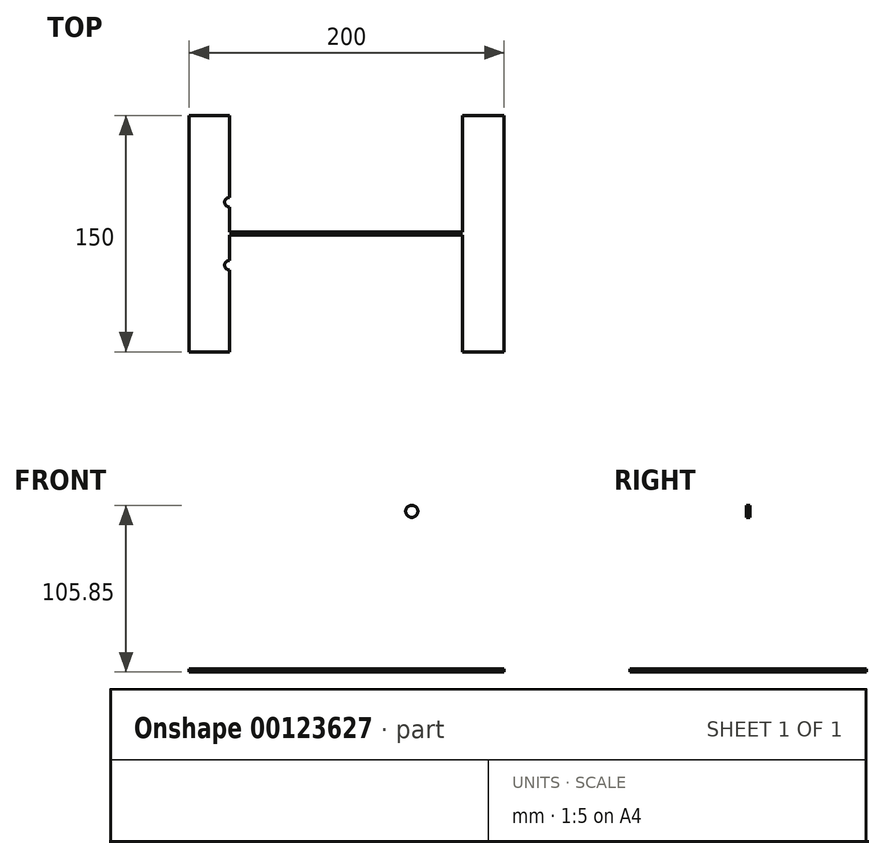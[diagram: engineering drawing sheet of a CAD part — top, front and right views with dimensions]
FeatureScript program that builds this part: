
annotation { "Feature Type Name" : "Feature", "Feature Type Description" : "" }
export const myFeature = defineFeature(function(context is Context, id is Id, definition is map)
    precondition{}
    {
        {
            var Q0;
            Q0=qCreatedBy(makeId("Top.planeOp"),FACE);
            var sketch = newSketch(context, id + "F0", { "sketchPlane" : qUnion([Q0])});
            skLineSegment(sketch, "E0.bottom", {"start": v(-99.5, 63.3) * mm, "end": v(100.5, 63.3) * mm});
            skLineSegment(sketch, "E0.top", {"start": v(-99.5, -86.7) * mm, "end": v(100.5, -86.7) * mm});
            skLineSegment(sketch, "E0.left", {"start": v(-99.5, 63.3) * mm, "end": v(-99.5, -86.7) * mm});
            skLineSegment(sketch, "E0.right", {"start": v(100.5, 63.3) * mm, "end": v(100.5, -86.7) * mm});
            skSolve(sketch);
        }
        {
            var Q0;
            Q0=makeQuery(id+"F0.imprint","IMPRINT",FACE,{"disambiguationData":[TD([[makeQuery(id+"F0.imprint","IMPRINT",EDGE,{"derivedFrom":sQuery(id+"F0.wireOp",EDGE,"E0.bottom")}),-1.0]])]});
            extrude(context, id + "F1", {"entities" : qUnion([Q0]), "depth" : 2 * mm});
        }
        {
            var Q0;
            Q0=makeQuery(id+"F1.opExtrude","CAP_FACE",FACE,{"disambiguationData":[OSD([sQuery(id+"F0.wireOp",EDGE,"E0.bottom"),sQuery(id+"F0.wireOp",EDGE,"E0.top"),sQuery(id+"F0.wireOp",EDGE,"E0.left"),sQuery(id+"F0.wireOp",EDGE,"E0.right")])],"isStart":false});
            var sketch = newSketch(context, id + "F2", { "sketchPlane" : qUnion([Q0])});
            skLineSegment(sketch, "E1.bottom", {"start": v(-99.5, 63.3) * mm, "end": v(-99.5, 63.3) * mm});
            skLineSegment(sketch, "E1.top", {"start": v(-99.5, -86.7) * mm, "end": v(-99.5, -86.7) * mm});
            skLineSegment(sketch, "E1.left", {"start": v(-99.5, 63.3) * mm, "end": v(-99.5, -86.7) * mm});
            skLineSegment(sketch, "E1.right", {"start": v(-99.5, 63.3) * mm, "end": v(-99.5, -86.7) * mm});
            skLineSegment(sketch, "E2.bottom", {"start": v(100.5, -86.7) * mm, "end": v(-99.5, -86.7) * mm});
            skLineSegment(sketch, "E2.top", {"start": v(100.5, 63.3) * mm, "end": v(-99.5, 63.3) * mm});
            skLineSegment(sketch, "E2.left", {"start": v(100.5, -86.7) * mm, "end": v(100.5, 63.3) * mm});
            skLineSegment(sketch, "E2.right", {"start": v(-99.5, -86.7) * mm, "end": v(-99.5, 63.3) * mm});
            skLineSegment(sketch, "E3", {"start": v(100.5, -11.7) * mm, "end": v(100.5, 8.3) * mm});
            skLineSegment(sketch, "E4", {"start": v(100.5, 8.3) * mm, "end": v(-99.5, 8.3) * mm});
            skLineSegment(sketch, "E5.MirrorCS", {"start": v(100.5, -31.7) * mm, "end": v(-99.5, -31.7) * mm});
            skLineSegment(sketch, "E6", {"start": v(74, 63.3) * mm, "end": v(74, -86.7) * mm});
            skLineSegment(sketch, "E7.MirrorCS", {"start": v(-74, 63.3) * mm, "end": v(-74, -86.7) * mm});
            skCircle(sketch, "E8", {"center": v(74, 8.3) * mm, "radius": 3 * mm});
            skCircle(sketch, "E9", {"center": v(74, -31.7) * mm, "radius": 3 * mm});
            skCircle(sketch, "E10.MirrorC", {"center": v(-74, -31.7) * mm, "radius": 3 * mm});
            skCircle(sketch, "E11.MirrorC", {"center": v(-74, 8.3) * mm, "radius": 3 * mm});
            skLineSegment(sketch, "E12.bottom", {"start": v(-99.5, -10.7) * mm, "end": v(100.5, -10.7) * mm});
            skLineSegment(sketch, "E12.top", {"start": v(-99.5, -12.7) * mm, "end": v(100.5, -12.7) * mm});
            skLineSegment(sketch, "E12.left", {"start": v(-99.5, -10.7) * mm, "end": v(-99.5, -12.7) * mm});
            skLineSegment(sketch, "E12.right", {"start": v(100.5, -10.7) * mm, "end": v(100.5, -12.7) * mm});
            skSolve(sketch);
        }
        {
            var Q0;
            {var subQ0=sQuery(id+"F2.wireOp",EDGE,"E12.bottom");var subQ1=sQuery(id+"F2.wireOp",EDGE,"E7.MirrorCS");var subQ2=makeQuery(id+"F2.imprint","INTERSECT",VERTEX,{"derivedFrom":[subQ1,subQ0]});Q0=makeQuery(id+"F2.imprint","IMPRINT",FACE,{"disambiguationData":[TD([[makeQuery(id+"F2.imprint","IMPRINT",EDGE,{"disambiguationData":[TD([[subQ2,-1.0]])],"derivedFrom":subQ1}),1.0]])]});}
            var Q1;
            {var subQ0=sQuery(id+"F2.wireOp",EDGE,"E12.bottom");var subQ1=sQuery(id+"F2.wireOp",EDGE,"E6");var subQ2=makeQuery(id+"F2.imprint","INTERSECT",VERTEX,{"derivedFrom":[subQ1,subQ0]});Q1=makeQuery(id+"F2.imprint","IMPRINT",FACE,{"disambiguationData":[TD([[makeQuery(id+"F2.imprint","IMPRINT",EDGE,{"disambiguationData":[TD([[subQ2,-1.0]])],"derivedFrom":subQ1}),1.0]])]});}
            var Q2;
            {var subQ5=sQuery(id+"F2.wireOp",EDGE,"E12.left");Q2=makeQuery(id+"F2.imprint","IMPRINT",FACE,{"disambiguationData":[TD([[makeQuery(id+"F2.imprint","IMPRINT",EDGE,{"derivedFrom":subQ5}),1.0]])]});}
            extrude(context, id + "F3", {"entities" : qUnion([Q0, Q1, Q2]), "operationType" : NewBodyOperationType.ADD, "depth" : 300 * mm});
        }
        {
            var Q0;
            Q0=makeQuery(id+"F3.opExtrude","SWEPT_FACE",FACE,{"disambiguationData":[OSD([sQuery(id+"F2.wireOp",EDGE,"E12.top")])]});
            var sketch = newSketch(context, id + "F4", { "sketchPlane" : qUnion([Q0])});
            skSolve(sketch);
        }
        {
            var Q0;
            {var subQ0=sQuery(id+"F2.wireOp",EDGE,"E10.MirrorC");var subQ1=sQuery(id+"F2.wireOp",EDGE,"E5.MirrorCS");var subQ2=makeQuery(id+"F2.imprint","INTERSECT",VERTEX,{"disambiguationData":[OD(0.0)],"derivedFrom":[subQ1,subQ0]});Q0=makeQuery(id+"F2.imprint","IMPRINT",FACE,{"disambiguationData":[TD([[makeQuery(id+"F2.imprint","IMPRINT",EDGE,{"disambiguationData":[TD([[subQ2,-1.0]])],"derivedFrom":subQ1}),1.0]])]});}
            var Q1;
            {var subQ0=sQuery(id+"F2.wireOp",EDGE,"E10.MirrorC");var subQ1=sQuery(id+"F2.wireOp",EDGE,"E5.MirrorCS");var subQ2=makeQuery(id+"F2.imprint","INTERSECT",VERTEX,{"disambiguationData":[OD(0.0)],"derivedFrom":[subQ1,subQ0]});Q1=makeQuery(id+"F2.imprint","IMPRINT",FACE,{"disambiguationData":[TD([[makeQuery(id+"F2.imprint","IMPRINT",EDGE,{"disambiguationData":[TD([[subQ2,-1.0]])],"derivedFrom":subQ1}),-1.0]])]});}
            var Q2;
            {var subQ0=sQuery(id+"F2.wireOp",EDGE,"E7.MirrorCS");var subQ1=sQuery(id+"F2.wireOp",EDGE,"E5.MirrorCS");var subQ2=makeQuery(id+"F2.imprint","INTERSECT",VERTEX,{"derivedFrom":[subQ1,subQ0]});Q2=makeQuery(id+"F2.imprint","IMPRINT",FACE,{"disambiguationData":[TD([[makeQuery(id+"F2.imprint","IMPRINT",EDGE,{"disambiguationData":[TD([[subQ2,-1.0]])],"derivedFrom":subQ1}),-1.0]])]});}
            var Q3;
            {var subQ0=sQuery(id+"F2.wireOp",EDGE,"E7.MirrorCS");var subQ1=sQuery(id+"F2.wireOp",EDGE,"E5.MirrorCS");var subQ2=makeQuery(id+"F2.imprint","INTERSECT",VERTEX,{"derivedFrom":[subQ1,subQ0]});Q3=makeQuery(id+"F2.imprint","IMPRINT",FACE,{"disambiguationData":[TD([[makeQuery(id+"F2.imprint","IMPRINT",EDGE,{"disambiguationData":[TD([[subQ2,-1.0]])],"derivedFrom":subQ1}),1.0]])]});}
            var Q4;
            {var subQ0=sQuery(id+"F2.wireOp",EDGE,"E6");var subQ1=sQuery(id+"F2.wireOp",EDGE,"E5.MirrorCS");var subQ2=makeQuery(id+"F2.imprint","INTERSECT",VERTEX,{"derivedFrom":[subQ1,subQ0]});Q4=makeQuery(id+"F2.imprint","IMPRINT",FACE,{"disambiguationData":[TD([[makeQuery(id+"F2.imprint","IMPRINT",EDGE,{"disambiguationData":[TD([[subQ2,-1.0]])],"derivedFrom":subQ1}),-1.0]])]});}
            var Q5;
            {var subQ0=sQuery(id+"F2.wireOp",EDGE,"E6");var subQ1=sQuery(id+"F2.wireOp",EDGE,"E5.MirrorCS");var subQ2=makeQuery(id+"F2.imprint","INTERSECT",VERTEX,{"derivedFrom":[subQ1,subQ0]});Q5=makeQuery(id+"F2.imprint","IMPRINT",FACE,{"disambiguationData":[TD([[makeQuery(id+"F2.imprint","IMPRINT",EDGE,{"disambiguationData":[TD([[subQ2,-1.0]])],"derivedFrom":subQ1}),1.0]])]});}
            var Q6;
            {var subQ0=sQuery(id+"F2.wireOp",EDGE,"E9");var subQ1=sQuery(id+"F2.wireOp",EDGE,"E5.MirrorCS");var subQ2=makeQuery(id+"F2.imprint","INTERSECT",VERTEX,{"disambiguationData":[OD(0.0)],"derivedFrom":[subQ1,subQ0]});Q6=makeQuery(id+"F2.imprint","IMPRINT",FACE,{"disambiguationData":[TD([[makeQuery(id+"F2.imprint","IMPRINT",EDGE,{"disambiguationData":[TD([[subQ2,-1.0]])],"derivedFrom":subQ1}),1.0]])]});}
            var Q7;
            {var subQ0=sQuery(id+"F2.wireOp",EDGE,"E9");var subQ1=sQuery(id+"F2.wireOp",EDGE,"E5.MirrorCS");var subQ2=makeQuery(id+"F2.imprint","INTERSECT",VERTEX,{"disambiguationData":[OD(0.0)],"derivedFrom":[subQ1,subQ0]});Q7=makeQuery(id+"F2.imprint","IMPRINT",FACE,{"disambiguationData":[TD([[makeQuery(id+"F2.imprint","IMPRINT",EDGE,{"disambiguationData":[TD([[subQ2,-1.0]])],"derivedFrom":subQ1}),-1.0]])]});}
            var Q8;
            {var subQ0=sQuery(id+"F2.wireOp",EDGE,"E11.MirrorC");var subQ1=sQuery(id+"F2.wireOp",EDGE,"E4");var subQ2=makeQuery(id+"F2.imprint","INTERSECT",VERTEX,{"disambiguationData":[OD(0.0)],"derivedFrom":[subQ1,subQ0]});Q8=makeQuery(id+"F2.imprint","IMPRINT",FACE,{"disambiguationData":[TD([[makeQuery(id+"F2.imprint","IMPRINT",EDGE,{"disambiguationData":[TD([[subQ2,-1.0]])],"derivedFrom":subQ1}),-1.0]])]});}
            var Q9;
            {var subQ0=sQuery(id+"F2.wireOp",EDGE,"E11.MirrorC");var subQ1=sQuery(id+"F2.wireOp",EDGE,"E4");var subQ2=makeQuery(id+"F2.imprint","INTERSECT",VERTEX,{"disambiguationData":[OD(0.0)],"derivedFrom":[subQ1,subQ0]});Q9=makeQuery(id+"F2.imprint","IMPRINT",FACE,{"disambiguationData":[TD([[makeQuery(id+"F2.imprint","IMPRINT",EDGE,{"disambiguationData":[TD([[subQ2,-1.0]])],"derivedFrom":subQ1}),1.0]])]});}
            var Q10;
            {var subQ0=sQuery(id+"F2.wireOp",EDGE,"E7.MirrorCS");var subQ1=sQuery(id+"F2.wireOp",EDGE,"E4");var subQ2=makeQuery(id+"F2.imprint","INTERSECT",VERTEX,{"derivedFrom":[subQ1,subQ0]});Q10=makeQuery(id+"F2.imprint","IMPRINT",FACE,{"disambiguationData":[TD([[makeQuery(id+"F2.imprint","IMPRINT",EDGE,{"disambiguationData":[TD([[subQ2,-1.0]])],"derivedFrom":subQ1}),1.0]])]});}
            var Q11;
            {var subQ0=sQuery(id+"F2.wireOp",EDGE,"E7.MirrorCS");var subQ1=sQuery(id+"F2.wireOp",EDGE,"E4");var subQ2=makeQuery(id+"F2.imprint","INTERSECT",VERTEX,{"derivedFrom":[subQ1,subQ0]});Q11=makeQuery(id+"F2.imprint","IMPRINT",FACE,{"disambiguationData":[TD([[makeQuery(id+"F2.imprint","IMPRINT",EDGE,{"disambiguationData":[TD([[subQ2,-1.0]])],"derivedFrom":subQ1}),-1.0]])]});}
            var Q12;
            {var subQ0=sQuery(id+"F2.wireOp",EDGE,"E8");var subQ1=sQuery(id+"F2.wireOp",EDGE,"E4");var subQ2=makeQuery(id+"F2.imprint","INTERSECT",VERTEX,{"disambiguationData":[OD(0.0)],"derivedFrom":[subQ1,subQ0]});Q12=makeQuery(id+"F2.imprint","IMPRINT",FACE,{"disambiguationData":[TD([[makeQuery(id+"F2.imprint","IMPRINT",EDGE,{"disambiguationData":[TD([[subQ2,-1.0]])],"derivedFrom":subQ1}),1.0]])]});}
            var Q13;
            {var subQ0=sQuery(id+"F2.wireOp",EDGE,"E8");var subQ1=sQuery(id+"F2.wireOp",EDGE,"E4");var subQ2=makeQuery(id+"F2.imprint","INTERSECT",VERTEX,{"disambiguationData":[OD(0.0)],"derivedFrom":[subQ1,subQ0]});Q13=makeQuery(id+"F2.imprint","IMPRINT",FACE,{"disambiguationData":[TD([[makeQuery(id+"F2.imprint","IMPRINT",EDGE,{"disambiguationData":[TD([[subQ2,-1.0]])],"derivedFrom":subQ1}),-1.0]])]});}
            var Q14;
            {var subQ0=sQuery(id+"F2.wireOp",EDGE,"E6");var subQ1=sQuery(id+"F2.wireOp",EDGE,"E4");var subQ2=makeQuery(id+"F2.imprint","INTERSECT",VERTEX,{"derivedFrom":[subQ1,subQ0]});Q14=makeQuery(id+"F2.imprint","IMPRINT",FACE,{"disambiguationData":[TD([[makeQuery(id+"F2.imprint","IMPRINT",EDGE,{"disambiguationData":[TD([[subQ2,-1.0]])],"derivedFrom":subQ1}),-1.0]])]});}
            var Q15;
            {var subQ0=sQuery(id+"F2.wireOp",EDGE,"E6");var subQ1=sQuery(id+"F2.wireOp",EDGE,"E4");var subQ2=makeQuery(id+"F2.imprint","INTERSECT",VERTEX,{"derivedFrom":[subQ1,subQ0]});Q15=makeQuery(id+"F2.imprint","IMPRINT",FACE,{"disambiguationData":[TD([[makeQuery(id+"F2.imprint","IMPRINT",EDGE,{"disambiguationData":[TD([[subQ2,-1.0]])],"derivedFrom":subQ1}),1.0]])]});}
            var Q16;
            Q16=sQuery(id+"F2.wireOp",EDGE,"E10.MirrorC");
            var Q17;
            Q17=sQuery(id+"F2.wireOp",EDGE,"E9");
            var Q18;
            Q18=sQuery(id+"F2.wireOp",EDGE,"E8");
            var Q19;
            Q19=sQuery(id+"F2.wireOp",EDGE,"E11.MirrorC");
            var Q20;
            Q20=makeQuery(id+"F1.opExtrude","CAP_FACE",FACE,{"disambiguationData":[OSD([sQuery(id+"F0.wireOp",EDGE,"E0.bottom"),sQuery(id+"F0.wireOp",EDGE,"E0.top"),sQuery(id+"F0.wireOp",EDGE,"E0.left"),sQuery(id+"F0.wireOp",EDGE,"E0.right")])],"isStart":true});
            extrude(context, id + "F5", {"entities" : qUnion([Q0, Q1, Q2, Q3, Q4, Q5, Q6, Q7, Q8, Q9, Q10, Q11, Q12, Q13, Q14, Q15]), "operationType" : NewBodyOperationType.REMOVE, "surfaceEntities" : qUnion([Q16, Q17, Q18, Q19]), "endBound" : BoundingType.THROUGH_ALL, "oppositeDirection" : true, "endBoundEntityFace" : qUnion([Q20]), "depth" : 2 * mm});
        }
        {
            var Q0;
            Q0=makeQuery(id+"F3.opExtrude","SWEPT_FACE",FACE,{"disambiguationData":[OSD([sQuery(id+"F2.wireOp",EDGE,"E12.bottom")])]});
            var sketch = newSketch(context, id + "F6", { "sketchPlane" : qUnion([Q0])});
            skLineSegment(sketch, "E13.bottom", {"start": v(-100.5, 302) * mm, "end": v(99.5, 302) * mm});
            skLineSegment(sketch, "E13.top", {"start": v(-100.5, 2) * mm, "end": v(99.5, 2) * mm});
            skLineSegment(sketch, "E13.left", {"start": v(-100.5, 302) * mm, "end": v(-100.5, 2) * mm});
            skLineSegment(sketch, "E13.right", {"start": v(99.5, 302) * mm, "end": v(99.5, 2) * mm});
            skCircle(sketch, "E14", {"center": v(-41.85, 102) * mm, "radius": 3.85 * mm});
            skCircle(sketch, "E15.MirrorC", {"center": v(36.95, 102) * mm, "radius": 3.85 * mm});
            skSolve(sketch);
        }
        {
            var Q0;
            Q0=makeQuery(id+"F6.imprint","IMPRINT",FACE,{"disambiguationData":[TD([[makeQuery(id+"F6.imprint","IMPRINT",EDGE,{"derivedFrom":sQuery(id+"F6.wireOp",EDGE,"E14")}),-1.0]])]});
            var Q1;
            Q1=makeQuery(id+"F6.imprint","IMPRINT",FACE,{"disambiguationData":[TD([[makeQuery(id+"F6.imprint","IMPRINT",EDGE,{"derivedFrom":sQuery(id+"F6.wireOp",EDGE,"E15.MirrorC")}),1.0]])]});
            var Q2;
            Q2=sQuery(id+"F6.wireOp",EDGE,"E14");
            var Q3;
            Q3=sQuery(id+"F6.wireOp",EDGE,"E15.MirrorC");
            extrude(context, id + "F7", {"entities" : qUnion([Q0, Q1]), "operationType" : NewBodyOperationType.REMOVE, "surfaceEntities" : qUnion([Q2, Q3]), "oppositeDirection" : true, "depth" : 2 * mm});
        }
    });
